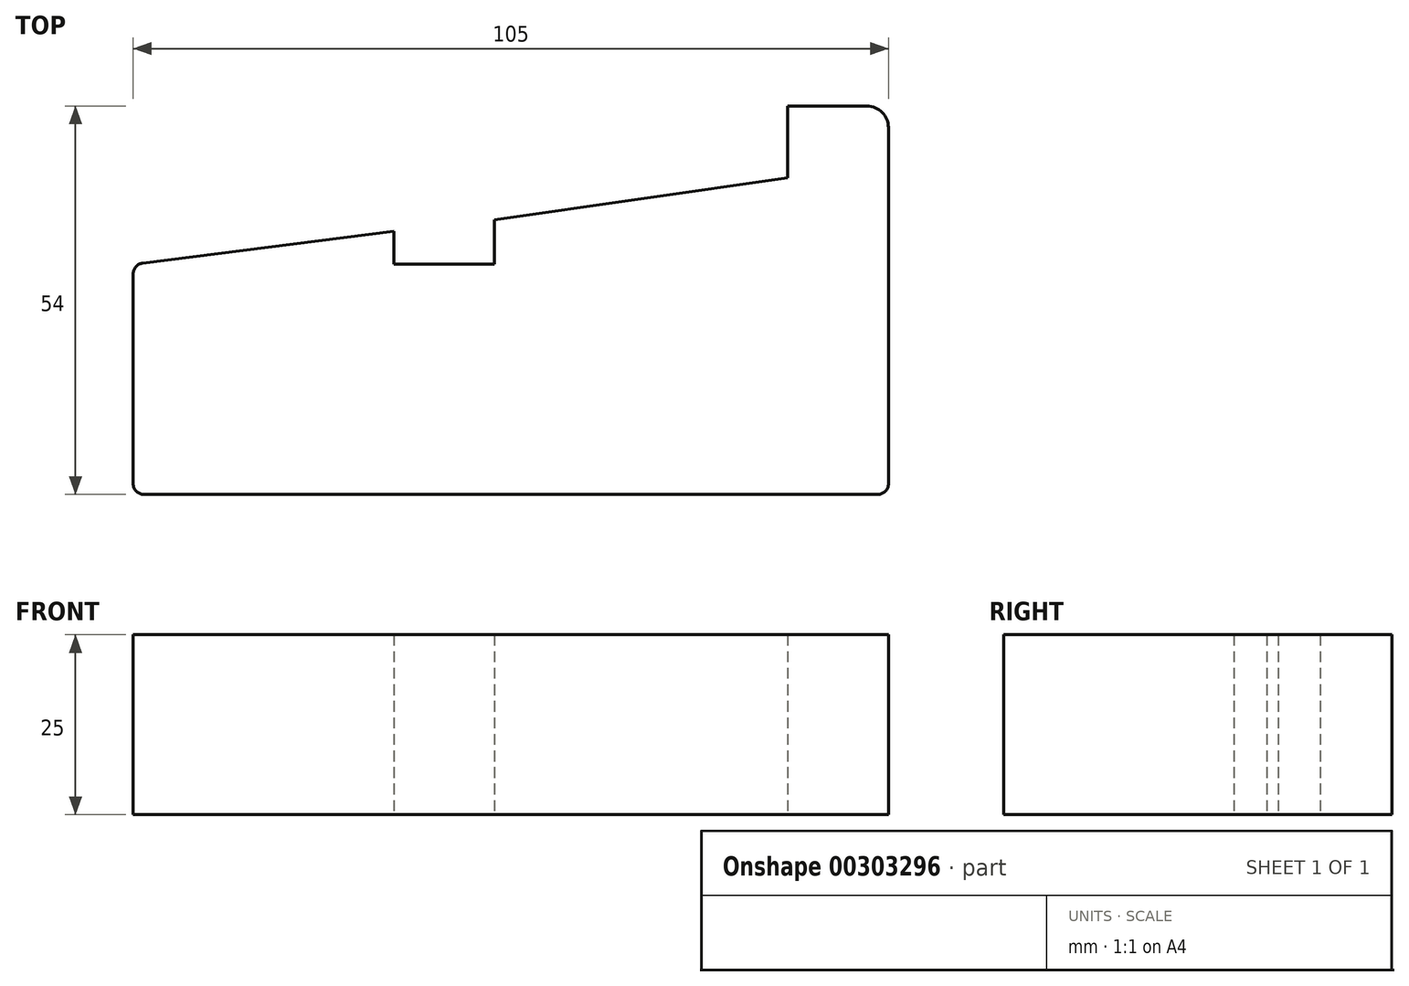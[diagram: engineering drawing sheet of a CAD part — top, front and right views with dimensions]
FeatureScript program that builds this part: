
annotation { "Feature Type Name" : "Feature", "Feature Type Description" : "" }
export const myFeature = defineFeature(function(context is Context, id is Id, definition is map)
    precondition{}
    {
        {
            var Q0;
            Q0=qCreatedBy(makeId("Top.planeOp"),FACE);
            var sketch = newSketch(context, id + "F0", { "sketchPlane" : qUnion([Q0])});
            skLineSegment(sketch, "E0", {"start": v(-56.33, 30.68) * mm, "end": v(-56.33, 1.5) * mm});
            skLineSegment(sketch, "E1", {"start": v(-54.83, 0) * mm, "end": v(47.17, 0) * mm});
            skLineSegment(sketch, "E2", {"start": v(48.67, 1.5) * mm, "end": v(48.67, 51) * mm});
            skLineSegment(sketch, "E3", {"start": v(45.67, 54) * mm, "end": v(34.67, 54) * mm});
            skLineSegment(sketch, "E4", {"start": v(34.67, 44) * mm, "end": v(34.67, 54) * mm});
            skLineSegment(sketch, "E5", {"start": v(34.67, 44) * mm, "end": v(-6.12, 38.21) * mm});
            skLineSegment(sketch, "E6", {"start": v(-6.12, 38.21) * mm, "end": v(-6.12, 32) * mm});
            skLineSegment(sketch, "E7", {"start": v(-6.12, 32) * mm, "end": v(-20.12, 32) * mm});
            skPoint(sketch, "E8.end.orphan", {"position": v(-55.12, 32) * mm});
            skLineSegment(sketch, "E9", {"start": v(-20.12, 32) * mm, "end": v(-20.12, 36.6) * mm});
            skLineSegment(sketch, "E10", {"start": v(-55.02, 32.17) * mm, "end": v(-20.12, 36.6) * mm});
            skPoint(sketch, "E11.visualSharp", {"position": v(48.67, 54) * mm});
            skArc(sketch, "E11.filletArc", {"start": v(48.67, 51) * mm, "mid": v(47.79, 53.12) * mm, "end": v(45.67, 54) * mm});
            skPoint(sketch, "E12.visualSharp", {"position": v(-56.33, 32) * mm});
            skArc(sketch, "E12.filletArc", {"start": v(-55.02, 32.17) * mm, "mid": v(-55.96, 31.67) * mm, "end": v(-56.33, 30.68) * mm});
            skPoint(sketch, "E13.visualSharp", {"position": v(-56.33, 0) * mm});
            skArc(sketch, "E13.filletArc", {"start": v(-56.33, 1.5) * mm, "mid": v(-55.9, 0.44) * mm, "end": v(-54.83, 0) * mm});
            skPoint(sketch, "E14.visualSharp", {"position": v(48.67, 0) * mm});
            skArc(sketch, "E14.filletArc", {"start": v(47.17, 0) * mm, "mid": v(48.23, 0.44) * mm, "end": v(48.67, 1.5) * mm});
            skSolve(sketch);
        }
        {
            var Q0;
            Q0 = qSketchRegion(id + "F0", true);
            extrude(context, id + "F1", {"entities" : qUnion([Q0]), "depth" : 25 * mm});
        }
    });
